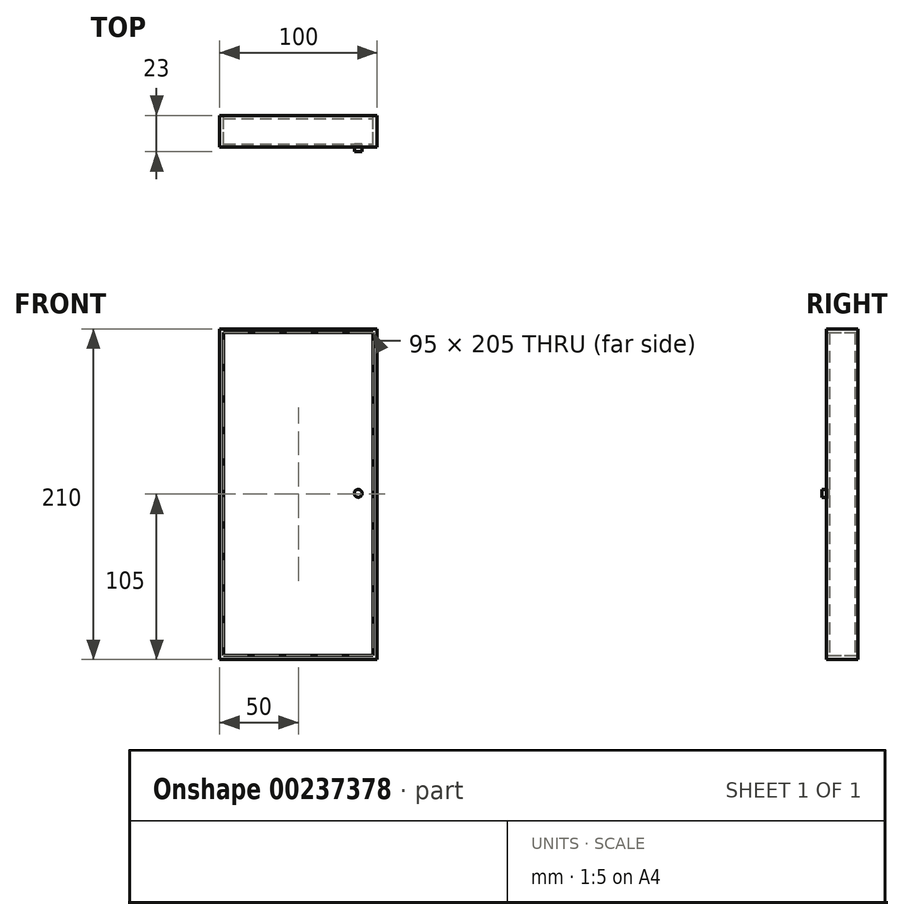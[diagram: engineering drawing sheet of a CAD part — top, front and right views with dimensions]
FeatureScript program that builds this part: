
annotation { "Feature Type Name" : "Feature", "Feature Type Description" : "" }
export const myFeature = defineFeature(function(context is Context, id is Id, definition is map)
    precondition{}
    {
        {
            var Q0;
            Q0=qCreatedBy(makeId("Front.planeOp"),FACE);
            var sketch = newSketch(context, id + "F0", { "sketchPlane" : qUnion([Q0])});
            skLineSegment(sketch, "E0.bottom", {"start": v(-100, 185) * mm, "end": v(0, 185) * mm});
            skLineSegment(sketch, "E0.top", {"start": v(-100, -25) * mm, "end": v(0, -25) * mm});
            skLineSegment(sketch, "E0.left", {"start": v(-100, 185) * mm, "end": v(-100, -25) * mm});
            skLineSegment(sketch, "E0.right", {"start": v(0, 185) * mm, "end": v(0, -25) * mm});
            skLineSegment(sketch, "E1.bottom", {"start": v(-100, 185) * mm, "end": v(-97.5, 185) * mm});
            skLineSegment(sketch, "E1.left", {"start": v(-100, 185) * mm, "end": v(-100, 182.5) * mm});
            skLineSegment(sketch, "E2.bottom", {"start": v(0, -25) * mm, "end": v(-2.5, -25) * mm});
            skLineSegment(sketch, "E2.left", {"start": v(0, -25) * mm, "end": v(0, -22.5) * mm});
            skLineSegment(sketch, "E3.bottom", {"start": v(-97.5, 182.5) * mm, "end": v(-2.5, 182.5) * mm});
            skLineSegment(sketch, "E3.top", {"start": v(-97.5, -22.5) * mm, "end": v(-2.5, -22.5) * mm});
            skLineSegment(sketch, "E3.left", {"start": v(-97.5, 182.5) * mm, "end": v(-97.5, -22.5) * mm});
            skLineSegment(sketch, "E3.right", {"start": v(-2.5, 182.5) * mm, "end": v(-2.5, -22.5) * mm});
            skSolve(sketch);
        }
        {
            var Q0;
            Q0=makeQuery(id+"F0.imprint","IMPRINT",FACE,{"disambiguationData":[TD([[makeQuery(id+"F0.imprint","IMPRINT",EDGE,{"derivedFrom":sQuery(id+"F0.wireOp",EDGE,"E0.bottom")}),-1.0]])]});
            extrude(context, id + "F1", {"entities" : qUnion([Q0]), "depth" : 10 * mm, "hasSecondDirection" : true, "secondDirectionOppositeDirection" : true, "secondDirectionDepth" : 10 * mm});
        }
        {
            var Q0;
            Q0=makeQuery(id+"F0.imprint","IMPRINT",FACE,{"disambiguationData":[TD([[makeQuery(id+"F0.imprint","IMPRINT",EDGE,{"derivedFrom":sQuery(id+"F0.wireOp",EDGE,"E3.bottom")}),-1.0]])]});
            extrude(context, id + "F2", {"entities" : qUnion([Q0]), "depth" : 8 * mm, "hasSecondDirection" : true, "secondDirectionOppositeDirection" : true, "secondDirectionDepth" : 8 * mm});
        }
        {
            var Q0;
            Q0=makeQuery(id+"F2.opExtrude","CAP_FACE",FACE,{"disambiguationData":[OSD([sQuery(id+"F0.wireOp",EDGE,"E3.bottom"),sQuery(id+"F0.wireOp",EDGE,"E3.top"),sQuery(id+"F0.wireOp",EDGE,"E3.left"),sQuery(id+"F0.wireOp",EDGE,"E3.right")])],"isStart":false});
            var sketch = newSketch(context, id + "F3", { "sketchPlane" : qUnion([Q0])});
            skCircle(sketch, "E4", {"center": v(-12.02, 80.49) * mm, "radius": 2.5 * mm});
            skSolve(sketch);
        }
        {
            var Q0;
            Q0=makeQuery(id+"F3.imprint","IMPRINT",FACE,{"disambiguationData":[TD([[makeQuery(id+"F3.imprint","IMPRINT",EDGE,{"derivedFrom":sQuery(id+"F3.wireOp",EDGE,"E4")}),1.0]])]});
            extrude(context, id + "F4", {"entities" : qUnion([Q0]), "depth" : 5 * mm});
        }
    });
